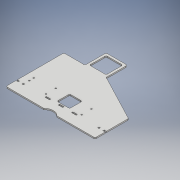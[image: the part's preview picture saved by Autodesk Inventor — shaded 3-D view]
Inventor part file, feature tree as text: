
AUTODESK INVENTOR PART (.ipt)
format: ipt  version: 2018 (Build 220112000, 112)  size: 212,480 bytes
history: native  units: mm
features: extrude x2, sketch x2, other x1, fillet x1
ambient origin geometry x8: Origin, YZ Plane, XZ Plane, XY Plane, X Axis, Y Axis, Z Axis, Center Point
bodies: Body1 (feature_tree)
feature tree (6):
  other  "Sólido1"
  extrude  "Extrusión1"  Depth=95.0mm
  fillet  "Empalme1"  Radius=95.0mm
  extrude  "Extrusión2"  Depth=400.0mm
  sketch  "Boceto1"  dims[d2=260.0mm d3=95.0mm d4=95.0mm]
  sketch  "Boceto2"  dims[d5=150.0mm d6=400.0mm d7=57.0mm d8=57.0mm d10=75.0mm d11=75.0mm d12=6.0mm d13=0.0mm d14=6.0mm d15=20.0mm d16=6.0mm d17=48.0mm d18=20.0mm d19=60.0mm d20=20.0mm d21=60.0mm d22=8.0mm d23=20.0mm d24=6.0mm d25=110.0mm d26=6.0mm d27=20.0mm d28=12.0mm d29=6.0mm d30=44.0mm d31=6.0mm d32=6.0mm d33=40.0mm d34=3.0mm d35=0.0mm d36=6.0mm d37=6.0mm]
